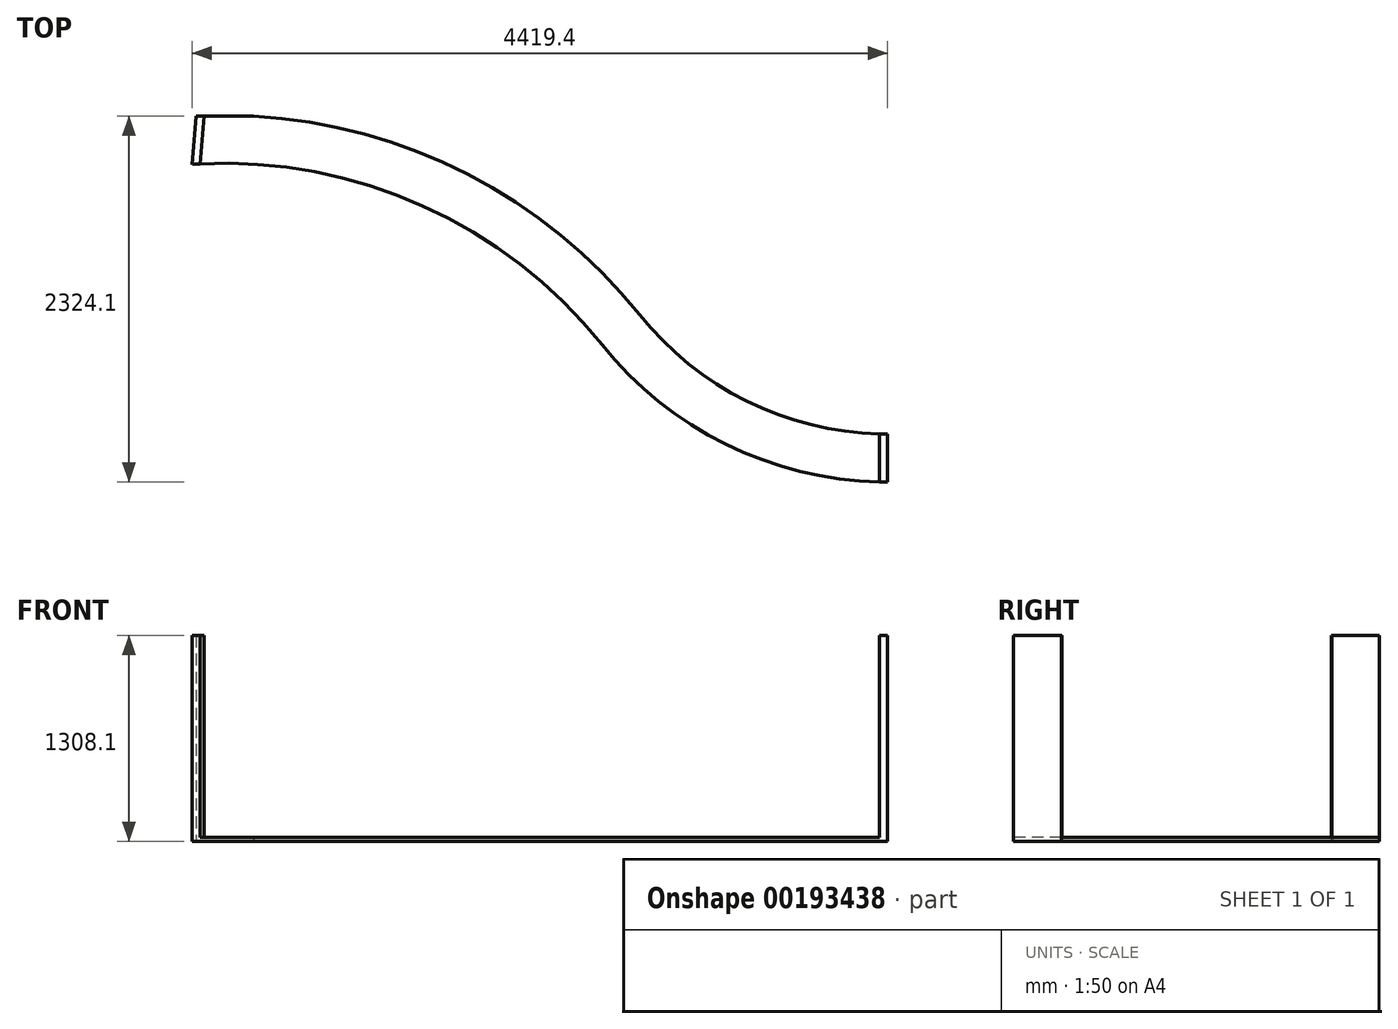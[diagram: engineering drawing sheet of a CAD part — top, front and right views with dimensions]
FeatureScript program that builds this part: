
annotation { "Feature Type Name" : "Feature", "Feature Type Description" : "" }
export const myFeature = defineFeature(function(context is Context, id is Id, definition is map)
    precondition{}
    {
        {
            var Q0;
            Q0=qCreatedBy(makeId("Top.planeOp"),FACE);
            var sketch = newSketch(context, id + "F0", { "sketchPlane" : qUnion([Q0])});
            skLineSegment(sketch, "E0", {"start": v(-2322.3, 99.74) * mm, "end": v(363.78, 99.74) * mm});
            skLineSegment(sketch, "E1", {"start": v(2078.28, -1614.76) * mm, "end": v(2078.28, -2224.36) * mm});
            skArc(sketch, "E2", {"start": v(2078.28, -1614.76) * mm, "mid": v(865.95, -1112.6) * mm, "end": v(363.78, 99.74) * mm});
            skArc(sketch, "E3.0", {"start": v(2078.28, -1919.56) * mm, "mid": v(1203.8, -1720.4) * mm, "end": v(501.84, -1162.16) * mm});
            skArc(sketch, "E4.0", {"start": v(2078.28, -2224.36) * mm, "mid": v(1071.81, -1995.13) * mm, "end": v(263.88, -1352.64) * mm});
            skLineSegment(sketch, "E5", {"start": v(-2322.3, 99.74) * mm, "end": v(-2341.12, -206.78) * mm});
            skPoint(sketch, "E6", {"position": v(-2322.3, 99.74) * mm});
            skArc(sketch, "E7", {"start": v(501.84, -1162.16) * mm, "mid": v(-757.31, -188.98) * mm, "end": v(-2322.3, 99.74) * mm});
            skArc(sketch, "E8.0", {"start": v(263.88, -1352.64) * mm, "mid": v(-898, -460.02) * mm, "end": v(-2341.12, -206.78) * mm});
            skPoint(sketch, "E9.orphan", {"position": v(-2399.79, -1162.16) * mm});
            skLineSegment(sketch, "E10", {"start": v(2078.28, 99.74) * mm, "end": v(0, -1978.55) * mm});
            skLineSegment(sketch, "E11", {"start": v(-2341.12, -206.78) * mm, "end": v(-2322.3, 99.74) * mm});
            skLineSegment(sketch, "E12", {"start": v(2078.28, -1614.76) * mm, "end": v(2052.9, -1614.09) * mm});
            skLineSegment(sketch, "E13.0", {"start": v(2052.88, -1614.09) * mm, "end": v(2052.88, -2223.26) * mm});
            skLineSegment(sketch, "E14", {"start": v(-2339.55, -181.22) * mm, "end": v(-2322.3, 99.74) * mm});
            skLineSegment(sketch, "E15", {"start": v(-2341.12, -206.78) * mm, "end": v(-2314.2, 100.17) * mm});
            skLineSegment(sketch, "E16", {"start": v(-2263, 102.5) * mm, "end": v(-2289.86, -203.77) * mm});
            skLineSegment(sketch, "E17", {"start": v(2027.48, -1918.93) * mm, "end": v(2027.48, -2223.8) * mm});
            skSolve(sketch);
        }
        {
            var Q0;
            {var subQ5=sQuery(id+"F0.wireOp",EDGE,"E7");var subQ9=sQuery(id+"F0.wireOp",EDGE,"E0");var subQ10=makeQuery(id+"F0.imprint","INTERSECT",VERTEX,{"derivedFrom":[subQ9,subQ5]});Q0=makeQuery(id+"F0.imprint","IMPRINT",FACE,{"disambiguationData":[TD([[makeQuery(id+"F0.imprint","IMPRINT",EDGE,{"disambiguationData":[TD([[subQ10,1.0]])],"derivedFrom":subQ9}),-1.0]])]});}
            extrude(context, id + "F1", {"entities" : qUnion([Q0]), "depth" : 25.4 * mm});
        }
        {
            var Q0;
            {var subQ0=sQuery(id+"F0.wireOp",EDGE,"E15");var subQ1=sQuery(id+"F0.wireOp",EDGE,"E0");var subQ2=makeQuery(id+"F0.imprint","INTERSECT",VERTEX,{"derivedFrom":[subQ1,subQ0]});Q0=makeQuery(id+"F0.imprint","IMPRINT",FACE,{"disambiguationData":[TD([[makeQuery(id+"F0.imprint","IMPRINT",EDGE,{"disambiguationData":[TD([[subQ2,-1.0]])],"derivedFrom":subQ1}),-1.0]])]});}
            extrude(context, id + "F2", {"entities" : qUnion([Q0]), "operationType" : NewBodyOperationType.ADD, "depth" : 1308.1 * mm});
        }
        {
            var Q0;
            {var subQ0=sQuery(id+"F0.wireOp",EDGE,"E17");Q0=makeQuery(id+"F0.imprint","IMPRINT",FACE,{"disambiguationData":[TD([[makeQuery(id+"F0.imprint","IMPRINT",EDGE,{"derivedFrom":subQ0}),-1.0]])]});}
            extrude(context, id + "F3", {"entities" : qUnion([Q0]), "operationType" : NewBodyOperationType.ADD, "depth" : 25.4 * mm});
        }
        {
            var Q0;
            {var subQ3=sQuery(id+"F0.wireOp",EDGE,"E17");Q0=makeQuery(id+"F0.imprint","IMPRINT",FACE,{"disambiguationData":[TD([[makeQuery(id+"F0.imprint","IMPRINT",EDGE,{"derivedFrom":subQ3}),1.0]])]});}
            extrude(context, id + "F4", {"entities" : qUnion([Q0]), "operationType" : NewBodyOperationType.ADD, "depth" : 1308.1 * mm});
        }
    });
